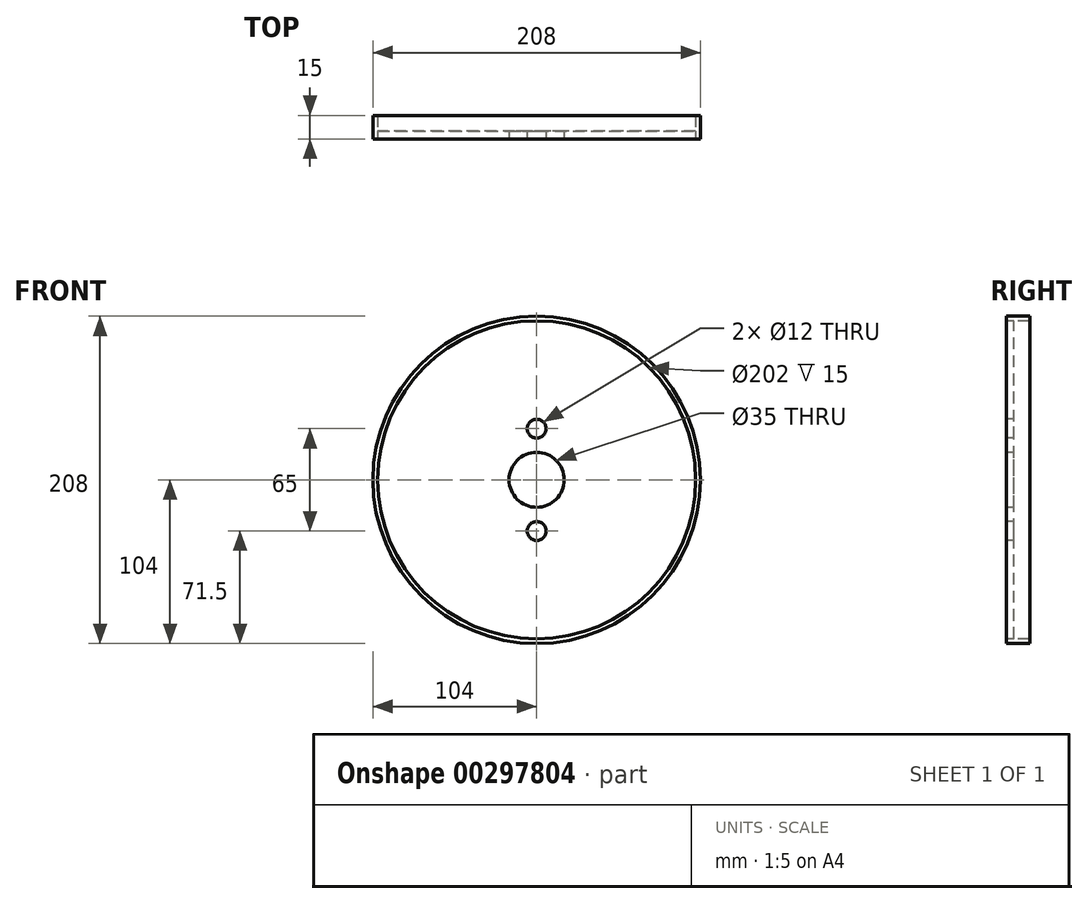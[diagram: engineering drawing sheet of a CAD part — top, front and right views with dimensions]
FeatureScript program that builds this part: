
annotation { "Feature Type Name" : "Feature", "Feature Type Description" : "" }
export const myFeature = defineFeature(function(context is Context, id is Id, definition is map)
    precondition{}
    {
        {
            var Q0;
            Q0=qCreatedBy(makeId("Front.planeOp"),FACE);
            var sketch = newSketch(context, id + "F0", { "sketchPlane" : qUnion([Q0])});
            skCircle(sketch, "E0", {"center": v(0, 0) * mm, "radius": 17.5 * mm});
            skCircle(sketch, "E1", {"center": v(0, 0) * mm, "radius": 101 * mm});
            skCircle(sketch, "E2.0", {"center": v(0, 0) * mm, "radius": 104 * mm});
            skCircle(sketch, "E3", {"center": v(0, 32.5) * mm, "radius": 6 * mm});
            skCircle(sketch, "E4", {"center": v(0, -32.5) * mm, "radius": 6 * mm});
            skLineSegment(sketch, "E5", {"start": v(-17.5, 0) * mm, "end": v(17.5, 0) * mm, "construction": true});
            skCircle(sketch, "E6", {"center": v(0, 32.5) * mm, "radius": 15 * mm});
            skCircle(sketch, "E7.MirrorC", {"center": v(0, -32.5) * mm, "radius": 15 * mm});
            skSolve(sketch);
        }
        {
            var Q0;
            Q0=makeQuery(id+"F0.imprint","IMPRINT",FACE,{"disambiguationData":[TD([[makeQuery(id+"F0.imprint","IMPRINT",EDGE,{"derivedFrom":sQuery(id+"F0.wireOp",EDGE,"E1")}),1.0]])]});
            var Q1;
            Q1=makeQuery(id+"F0.imprint","IMPRINT",FACE,{"disambiguationData":[TD([[makeQuery(id+"F0.imprint","IMPRINT",EDGE,{"derivedFrom":sQuery(id+"F0.wireOp",EDGE,"E3")}),-1.0]])]});
            var Q2;
            Q2=makeQuery(id+"F0.imprint","IMPRINT",FACE,{"disambiguationData":[TD([[makeQuery(id+"F0.imprint","IMPRINT",EDGE,{"derivedFrom":sQuery(id+"F0.wireOp",EDGE,"E4")}),-1.0]])]});
            extrude(context, id + "F1", {"entities" : qUnion([Q0, Q1, Q2]), "oppositeDirection" : true, "depth" : 5 * mm});
        }
        {
            var Q0;
            Q0=makeQuery(id+"F0.imprint","IMPRINT",FACE,{"disambiguationData":[TD([[makeQuery(id+"F0.imprint","IMPRINT",EDGE,{"derivedFrom":sQuery(id+"F0.wireOp",EDGE,"E1")}),-1.0]])]});
            extrude(context, id + "F2", {"entities" : qUnion([Q0]), "oppositeDirection" : true, "depth" : 15 * mm});
        }
    });
